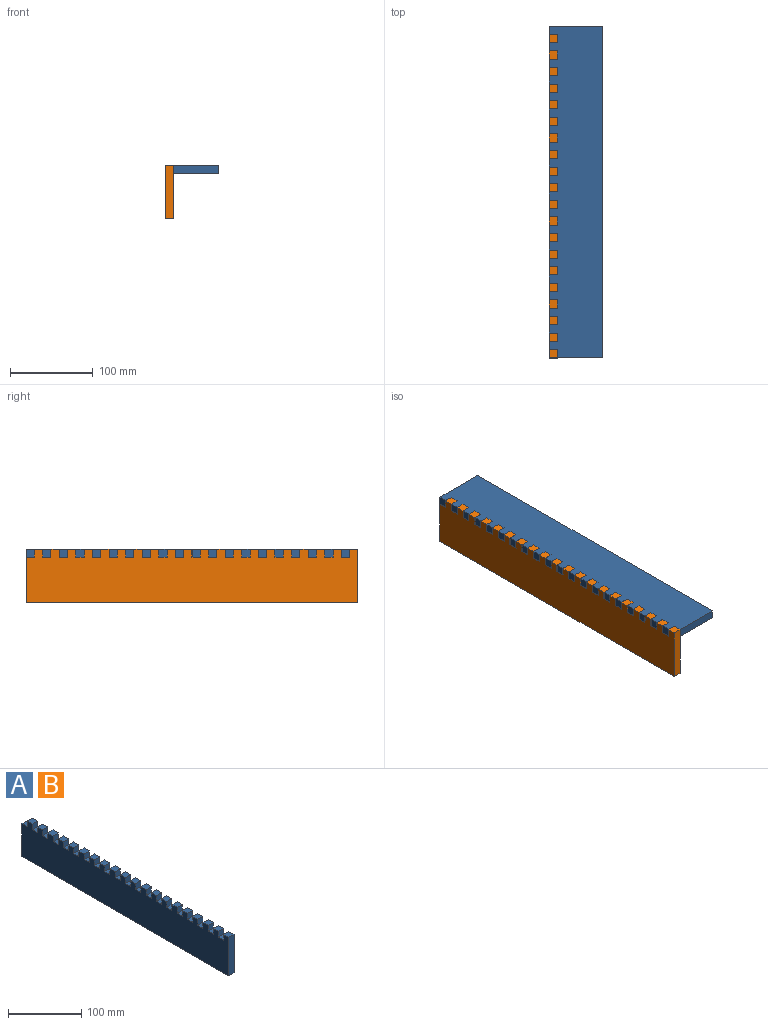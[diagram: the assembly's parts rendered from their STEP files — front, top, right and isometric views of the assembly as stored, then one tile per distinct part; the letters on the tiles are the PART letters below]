
ASSEMBLY  parts=2 mates=1
PART A: 84 faces, bbox 10x400x64.5 mm
  f0: plane 10x9.52mm, normal (0,-1,0), area 95.2mm2, adj f1,f81,f82,f83
  f1: plane 10x10mm, normal (0,0,1), area 100mm2, adj f0,f2,f82,f83
  f2: plane 10x9.52mm, normal (0,1,0), area 95.2mm2, adj f1,f3,f82,f83
  f3: plane 10x10mm, normal (0,0,1), area 100mm2, adj f2,f4,f82,f83
  f4: plane 10x9.52mm, normal (0,-1,0), area 95.2mm2, adj f3,f5,f82,f83
  f5: plane 10x10mm, normal (0,0,1), area 100mm2, adj f4,f6,f82,f83
  f6: plane 10x9.52mm, normal (0,1,0), area 95.2mm2, adj f5,f7,f82,f83
  f7: plane 10x10mm, normal (0,0,1), area 100mm2, adj f6,f8,f82,f83
  f8: plane 10x9.52mm, normal (0,-1,0), area 95.2mm2, adj f7,f9,f82,f83
  f9: plane 10x10mm, normal (0,0,1), area 100mm2, adj f8,f10,f82,f83
  f10: plane 10x9.52mm, normal (0,1,0), area 95.2mm2, adj f9,f11,f82,f83
  f11: plane 10x10mm, normal (0,0,1), area 100mm2, adj f10,f12,f82,f83
  f12: plane 10x9.52mm, normal (0,-1,0), area 95.2mm2, adj f11,f13,f82,f83
  f13: plane 10x10mm, normal (0,0,1), area 100mm2, adj f12,f14,f82,f83
  f14: plane 10x9.52mm, normal (0,1,0), area 95.2mm2, adj f13,f15,f82,f83
  f15: plane 10x10mm, normal (0,0,1), area 100mm2, adj f14,f16,f82,f83
  f16: plane 10x9.52mm, normal (0,-1,0), area 95.2mm2, adj f15,f17,f82,f83
  f17: plane 10x10mm, normal (0,0,1), area 100mm2, adj f16,f18,f82,f83
  f18: plane 10x9.52mm, normal (0,1,0), area 95.2mm2, adj f17,f19,f82,f83
  f19: plane 10x10mm, normal (0,0,1), area 100mm2, adj f18,f20,f82,f83
  f20: plane 64.52x10mm, normal (0,-1,0), area 645.2mm2, adj f19,f21,f82,f83
  f21: plane 400x10mm, normal (0,0,-1), area 4000mm2, adj f20,f22,f82,f83
  f22: plane 55x10mm, normal (0,1,0), area 550mm2, adj f21,f23,f82,f83
  f23: plane 10x10mm, normal (0,0,1), area 100mm2, adj f22,f24,f82,f83
  f24: plane 10x9.52mm, normal (0,1,0), area 95.2mm2, adj f23,f25,f82,f83
  f25: plane 10x10mm, normal (0,0,1), area 100mm2, adj f24,f26,f82,f83
  f26: plane 10x9.52mm, normal (0,-1,0), area 95.2mm2, adj f25,f27,f82,f83
  f27: plane 10x10mm, normal (0,0,1), area 100mm2, adj f26,f28,f82,f83
  f28: plane 10x9.52mm, normal (0,1,0), area 95.2mm2, adj f27,f29,f82,f83
  f29: plane 10x10mm, normal (0,0,1), area 100mm2, adj f28,f30,f82,f83
  f30: plane 10x9.52mm, normal (0,-1,0), area 95.2mm2, adj f29,f31,f82,f83
  f31: plane 10x10mm, normal (0,0,1), area 100mm2, adj f30,f32,f82,f83
  f32: plane 10x9.52mm, normal (0,1,0), area 95.2mm2, adj f31,f33,f82,f83
  f33: plane 10x10mm, normal (0,0,1), area 100mm2, adj f32,f34,f82,f83
  f34: plane 10x9.52mm, normal (0,-1,0), area 95.2mm2, adj f33,f35,f82,f83
  f35: plane 10x10mm, normal (0,0,1), area 100mm2, adj f34,f36,f82,f83
  f36: plane 10x9.52mm, normal (0,1,0), area 95.2mm2, adj f35,f37,f82,f83
  f37: plane 10x10mm, normal (0,0,1), area 100mm2, adj f36,f38,f82,f83
  f38: plane 10x9.52mm, normal (0,-1,0), area 95.2mm2, adj f37,f39,f82,f83
  f39: plane 10x10mm, normal (0,0,1), area 100mm2, adj f38,f40,f82,f83
  f40: plane 10x9.52mm, normal (0,1,0), area 95.2mm2, adj f39,f41,f82,f83
  f41: plane 10x10mm, normal (0,0,1), area 100mm2, adj f40,f42,f82,f83
  f42: plane 10x9.52mm, normal (0,-1,0), area 95.2mm2, adj f41,f43,f82,f83
  f43: plane 10x10mm, normal (0,0,1), area 100mm2, adj f42,f44,f82,f83
  f44: plane 10x9.52mm, normal (0,1,0), area 95.2mm2, adj f43,f45,f82,f83
  f45: plane 10x10mm, normal (0,0,1), area 100mm2, adj f44,f46,f82,f83
  f46: plane 10x9.52mm, normal (0,-1,0), area 95.2mm2, adj f45,f47,f82,f83
  f47: plane 10x10mm, normal (0,0,1), area 100mm2, adj f46,f48,f82,f83
  f48: plane 10x9.52mm, normal (0,1,0), area 95.2mm2, adj f47,f49,f82,f83
  f49: plane 10x10mm, normal (0,0,1), area 100mm2, adj f48,f50,f82,f83
  f50: plane 10x9.52mm, normal (0,-1,0), area 95.2mm2, adj f49,f51,f82,f83
  f51: plane 10x10mm, normal (0,0,1), area 100mm2, adj f50,f52,f82,f83
  f52: plane 10x9.52mm, normal (0,1,0), area 95.2mm2, adj f51,f53,f82,f83
  f53: plane 10x10mm, normal (0,0,1), area 100mm2, adj f52,f54,f82,f83
  f54: plane 10x9.52mm, normal (0,-1,0), area 95.2mm2, adj f53,f55,f82,f83
  f55: plane 10x10mm, normal (0,0,1), area 100mm2, adj f54,f56,f82,f83
  f56: plane 10x9.52mm, normal (0,1,0), area 95.2mm2, adj f55,f57,f82,f83
  f57: plane 10x10mm, normal (0,0,1), area 100mm2, adj f56,f58,f82,f83
  f58: plane 10x9.52mm, normal (0,-1,0), area 95.2mm2, adj f57,f59,f82,f83
  f59: plane 10x10mm, normal (0,0,1), area 100mm2, adj f58,f60,f82,f83
  f60: plane 10x9.52mm, normal (0,1,0), area 95.2mm2, adj f59,f61,f82,f83
  f61: plane 10x10mm, normal (0,0,1), area 100mm2, adj f60,f62,f82,f83
  f62: plane 10x9.52mm, normal (0,-1,0), area 95.2mm2, adj f61,f63,f82,f83
  f63: plane 10x10mm, normal (0,0,1), area 100mm2, adj f62,f64,f82,f83
  f64: plane 10x9.52mm, normal (0,1,0), area 95.2mm2, adj f63,f65,f82,f83
  f65: plane 10x10mm, normal (0,0,1), area 100mm2, adj f64,f66,f82,f83
  f66: plane 10x9.52mm, normal (0,-1,0), area 95.2mm2, adj f65,f67,f82,f83
  f67: plane 10x10mm, normal (0,0,1), area 100mm2, adj f66,f68,f82,f83
  f68: plane 10x9.52mm, normal (0,1,0), area 95.2mm2, adj f67,f69,f82,f83
  f69: plane 10x10mm, normal (0,0,1), area 100mm2, adj f68,f70,f82,f83
  f70: plane 10x9.52mm, normal (0,-1,0), area 95.2mm2, adj f69,f71,f82,f83
  f71: plane 10x10mm, normal (0,0,1), area 100mm2, adj f70,f72,f82,f83
  f72: plane 10x9.52mm, normal (0,1,0), area 95.2mm2, adj f71,f73,f82,f83
  f73: plane 10x10mm, normal (0,0,1), area 100mm2, adj f72,f74,f82,f83
  f74: plane 10x9.52mm, normal (0,-1,0), area 95.2mm2, adj f73,f75,f82,f83
  f75: plane 10x10mm, normal (0,0,1), area 100mm2, adj f74,f76,f82,f83
  f76: plane 10x9.52mm, normal (0,1,0), area 95.2mm2, adj f75,f77,f82,f83
  f77: plane 10x10mm, normal (0,0,1), area 100mm2, adj f76,f78,f82,f83
  f78: plane 10x9.52mm, normal (0,-1,0), area 95.2mm2, adj f77,f79,f82,f83
  f79: plane 10x10mm, normal (0,0,1), area 100mm2, adj f78,f80,f82,f83
  f80: plane 10x9.52mm, normal (0,1,0), area 95.2mm2, adj f79,f81,f82,f83
  f81: plane 10x10mm, normal (0,0,1), area 100mm2, adj f0,f80,f82,f83
  f82: plane 400x64.52mm, normal (1,0,0), area 23903.3mm2, adj f0,f1,f2,f3,f4,f5,f6,f7
  f83: plane 400x64.52mm, normal (-1,0,0), area 23903.3mm2, adj f0,f1,f2,f3,f4,f5,f6,f7
PART B: same geometry as A
PLACE A rot(axis=(-0.71,0,0.71),180deg) t=(5.24,311.2,4.76)mm
PLACE B at identity
MATE fastened A.f22 <-> B.f20  axis (0,-1,0) through (10,-44.4,4.76)mm
